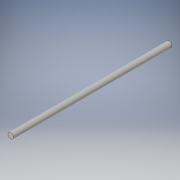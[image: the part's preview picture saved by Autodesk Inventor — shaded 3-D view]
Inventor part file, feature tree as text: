
AUTODESK INVENTOR PART (.ipt)
format: ipt  version: 2016 (Build 200138000, 138)  size: 86,016 bytes
history: native  units: in
note: dims shown in document units (in); Inventor stores cm internally (conversion verified against a paired STEP export)
features: extrude x1, sketch x1
ambient origin geometry x8: Origin, YZ Plane, XZ Plane, XY Plane, X Axis, Y Axis, Z Axis, Center Point
bodies: Solid1 (feature_tree)
feature tree (2):
  extrude  "Extrusion1"  Depth=4.0in TaperAngle=0.0deg
  sketch  "Sketch1"  dims[d0=0.14in d1=4.0in d2=0.0in]
